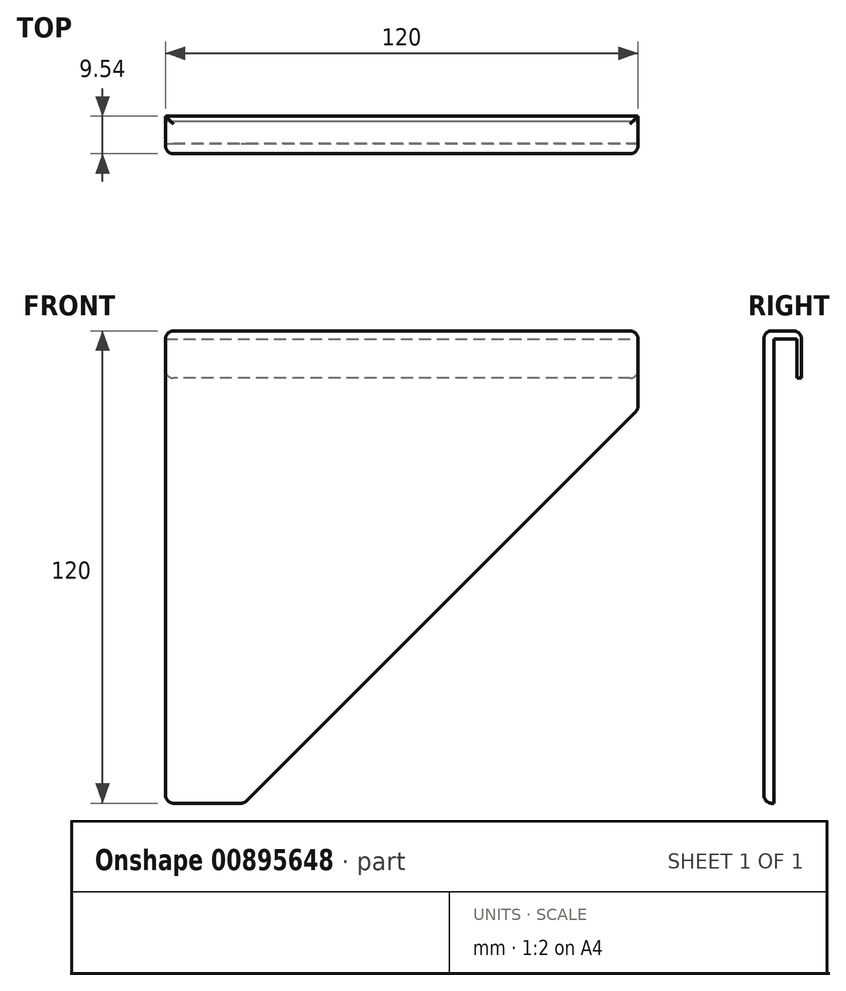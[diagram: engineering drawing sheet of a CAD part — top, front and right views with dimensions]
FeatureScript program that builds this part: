
annotation { "Feature Type Name" : "Feature", "Feature Type Description" : "" }
export const myFeature = defineFeature(function(context is Context, id is Id, definition is map)
    precondition{}
    {
        {
            var Q0;
            Q0=qCreatedBy(makeId("Front.planeOp"),FACE);
            var sketch = newSketch(context, id + "F0", { "sketchPlane" : qUnion([Q0])});
            skLineSegment(sketch, "E0", {"start": v(0, 0) * mm, "end": v(0, 120) * mm});
            skLineSegment(sketch, "E1", {"start": v(0, 120) * mm, "end": v(120, 120) * mm});
            skLineSegment(sketch, "E2", {"start": v(120, 120) * mm, "end": v(120, 100) * mm});
            skLineSegment(sketch, "E3", {"start": v(0, 0) * mm, "end": v(20, 0) * mm});
            skLineSegment(sketch, "E4", {"start": v(20, 0) * mm, "end": v(120, 100) * mm});
            skSolve(sketch);
        }
        {
            var Q0;
            Q0=makeQuery(id+"F0.imprint","IMPRINT",FACE,{"disambiguationData":[TD([[makeQuery(id+"F0.imprint","IMPRINT",EDGE,{"derivedFrom":sQuery(id+"F0.wireOp",EDGE,"E0")}),-1.0]])]});
            var sketch = newSketch(context, id + "F1", { "sketchPlane" : qUnion([Q0])});
            skLineSegment(sketch, "E5.bottom", {"start": v(120, 120) * mm, "end": v(0, 120) * mm});
            skLineSegment(sketch, "E5.top", {"start": v(120, 118) * mm, "end": v(0, 118) * mm});
            skLineSegment(sketch, "E5.left", {"start": v(120, 120) * mm, "end": v(120, 118) * mm});
            skLineSegment(sketch, "E5.right", {"start": v(0, 120) * mm, "end": v(0, 118) * mm});
            skSolve(sketch);
        }
        {
            var Q0;
            Q0 = qSketchRegion(id + "F1", true);
            extrude(context, id + "F2", {"entities" : qUnion([Q0]), "oppositeDirection" : true, "depth" : 7 * mm, "offsetDistance" : 25 * mm});
        }
        {
            var Q0;
            Q0=makeQuery(id+"F0.imprint","IMPRINT",FACE,{"disambiguationData":[TD([[makeQuery(id+"F0.imprint","IMPRINT",EDGE,{"derivedFrom":sQuery(id+"F0.wireOp",EDGE,"E0")}),-1.0]])]});
            extrude(context, id + "F3", {"entities" : qUnion([Q0]), "operationType" : NewBodyOperationType.ADD, "depth" : 2.54 * mm, "offsetDistance" : 25 * mm});
        }
        {
            var Q0;
            Q0=makeQuery(id+"F2.opExtrude","SWEPT_FACE",FACE,{"disambiguationData":[OSD([sQuery(id+"F1.wireOp",EDGE,"E5.top")])]});
            var sketch = newSketch(context, id + "F4", { "sketchPlane" : qUnion([Q0])});
            skLineSegment(sketch, "E6.bottom", {"start": v(0, -7) * mm, "end": v(120, -7) * mm});
            skLineSegment(sketch, "E6.top", {"start": v(0, -5.8) * mm, "end": v(120, -5.8) * mm});
            skLineSegment(sketch, "E6.left", {"start": v(0, -7) * mm, "end": v(0, -5.8) * mm});
            skLineSegment(sketch, "E6.right", {"start": v(120, -7) * mm, "end": v(120, -5.8) * mm});
            skSolve(sketch);
        }
        {
            var Q0;
            Q0=makeQuery(id+"F4.imprint","IMPRINT",FACE,{"disambiguationData":[TD([[makeQuery(id+"F4.imprint","IMPRINT",EDGE,{"derivedFrom":sQuery(id+"F4.wireOp",EDGE,"E6.bottom")}),-1.0]])]});
            extrude(context, id + "F5", {"entities" : qUnion([Q0]), "operationType" : NewBodyOperationType.ADD, "depth" : 10 * mm, "offsetDistance" : 25 * mm});
        }
        {
            var Q0;
            Q0=makeQuery(id+"F3.opExtrude","SWEPT_EDGE",EDGE,{"disambiguationData":[OSD([sQuery(id+"F0.wireOp",EDGE,"E0"),sQuery(id+"F0.wireOp",EDGE,"E3")])]});
            var Q1;
            Q1=makeQuery(id+"F3.opExtrude","SWEPT_EDGE",EDGE,{"disambiguationData":[OSD([sQuery(id+"F0.wireOp",EDGE,"E3"),sQuery(id+"F0.wireOp",EDGE,"E4")])]});
            var Q2;
            Q2=makeQuery(id+"F3.opExtrude","SWEPT_EDGE",EDGE,{"disambiguationData":[OSD([sQuery(id+"F0.wireOp",EDGE,"E2"),sQuery(id+"F0.wireOp",EDGE,"E4")])]});
            var Q3;
            Q3=makeQuery(id+"F3.boolean.opBoolean","MERGE",EDGE,{"derivedFrom":[makeQuery(id+"F2.opExtrude","SWEPT_EDGE",EDGE,{"disambiguationData":[OSD([sQuery(id+"F1.wireOp",EDGE,"E5.bottom"),sQuery(id+"F1.wireOp",EDGE,"E5.right")])]}),makeQuery(id+"F3.opExtrude","SWEPT_EDGE",EDGE,{"disambiguationData":[OSD([sQuery(id+"F0.wireOp",EDGE,"E0"),sQuery(id+"F0.wireOp",EDGE,"E1")])]})]});
            var Q4;
            Q4=makeQuery(id+"F3.boolean.opBoolean","MERGE",EDGE,{"derivedFrom":[makeQuery(id+"F2.opExtrude","SWEPT_EDGE",EDGE,{"disambiguationData":[OSD([sQuery(id+"F1.wireOp",EDGE,"E5.bottom"),sQuery(id+"F1.wireOp",EDGE,"E5.left")])]}),makeQuery(id+"F3.opExtrude","SWEPT_EDGE",EDGE,{"disambiguationData":[OSD([sQuery(id+"F0.wireOp",EDGE,"E1"),sQuery(id+"F0.wireOp",EDGE,"E2")])]})]});
            var Q5;
            Q5=makeQuery(id+"F5.opExtrude","CAP_EDGE",EDGE,{"disambiguationData":[OSD([sQuery(id+"F4.wireOp",EDGE,"E6.right")])],"isStart":false});
            var Q6;
            Q6=makeQuery(id+"F5.opExtrude","CAP_EDGE",EDGE,{"disambiguationData":[OSD([sQuery(id+"F4.wireOp",EDGE,"E6.left")])],"isStart":false});
            var Q7;
            Q7=makeQuery(id+"F3.opExtrude","CAP_EDGE",EDGE,{"disambiguationData":[OSD([sQuery(id+"F0.wireOp",EDGE,"E0")])],"isStart":false});
            var Q8;
            Q8=makeQuery(id+"F3.opExtrude","CAP_EDGE",EDGE,{"disambiguationData":[OSD([sQuery(id+"F0.wireOp",EDGE,"E1")])],"isStart":false});
            var Q9;
            Q9=makeQuery(id+"F3.opExtrude","CAP_EDGE",EDGE,{"disambiguationData":[OSD([sQuery(id+"F0.wireOp",EDGE,"E2")])],"isStart":false});
            var Q10;
            Q10=makeQuery(id+"F3.opExtrude","CAP_EDGE",EDGE,{"disambiguationData":[OSD([sQuery(id+"F0.wireOp",EDGE,"E4")])],"isStart":false});
            var Q11;
            Q11=makeQuery(id+"F3.opExtrude","CAP_EDGE",EDGE,{"disambiguationData":[OSD([sQuery(id+"F0.wireOp",EDGE,"E3")])],"isStart":false});
            var Q12;
            Q12=makeQuery(id+"F2.opExtrude","CAP_EDGE",EDGE,{"disambiguationData":[OSD([sQuery(id+"F1.wireOp",EDGE,"E5.top")])],"isStart":true});
            var Q13;
            Q13=makeQuery(id+"F5.opExtrude","CAP_EDGE",EDGE,{"disambiguationData":[OSD([sQuery(id+"F4.wireOp",EDGE,"E6.top")])],"isStart":true});
            var Q14;
            Q14=makeQuery(id+"F2.opExtrude","CAP_EDGE",EDGE,{"disambiguationData":[OSD([sQuery(id+"F1.wireOp",EDGE,"E5.bottom")])],"isStart":false});
            fillet(context, id + "F6", {"entities" : qUnion([Q0, Q1, Q2, Q3, Q4, Q5, Q6, Q7, Q8, Q9, Q10, Q11, Q12, Q13, Q14]), "radius" : 2 * mm, "tangentPropagation" : true, "allowEdgeOverflow" : false});
        }
    });
